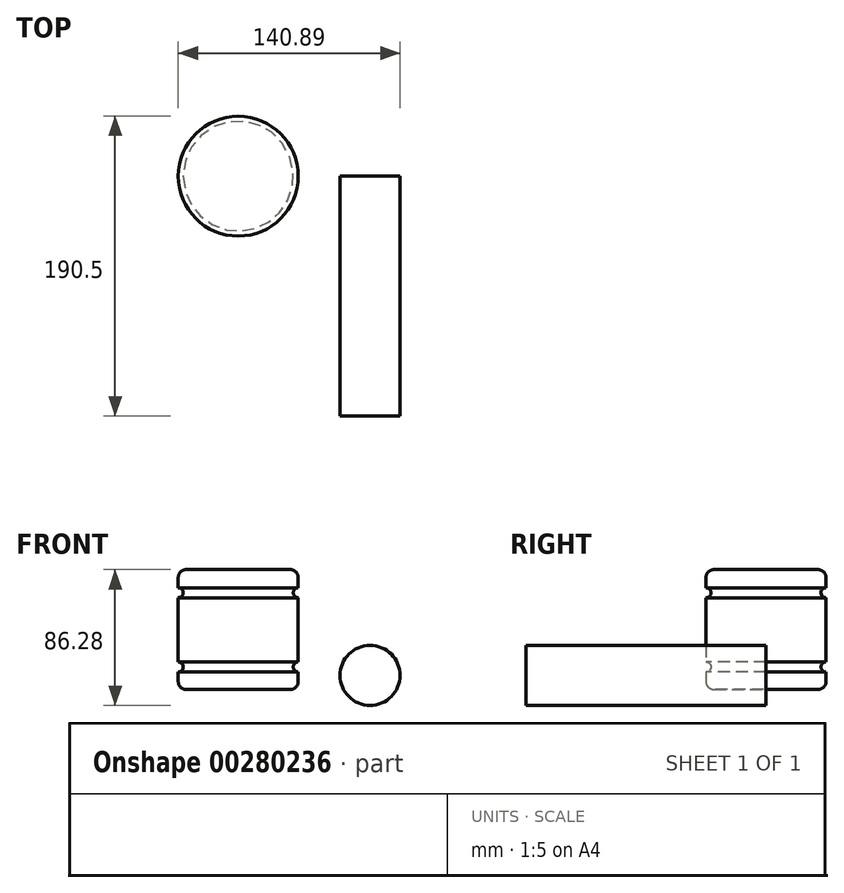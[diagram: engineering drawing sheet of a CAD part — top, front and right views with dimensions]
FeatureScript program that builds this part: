
annotation { "Feature Type Name" : "Feature", "Feature Type Description" : "" }
export const myFeature = defineFeature(function(context is Context, id is Id, definition is map)
    precondition{}
    {
        {
            var Q0;
            Q0=qCreatedBy(makeId("Front.planeOp"),FACE);
            var sketch = newSketch(context, id + "F0", { "sketchPlane" : qUnion([Q0])});
            skLineSegment(sketch, "E0.bottom", {"start": v(0, 0) * mm, "end": v(-38.1, 0) * mm});
            skLineSegment(sketch, "E0.top", {"start": v(0, 76.2) * mm, "end": v(-38.1, 76.2) * mm});
            skLineSegment(sketch, "E0.left", {"start": v(0, 0) * mm, "end": v(0, 76.2) * mm});
            skLineSegment(sketch, "E0.right", {"start": v(-38.1, 0) * mm, "end": v(-38.1, 76.2) * mm});
            skCircle(sketch, "E1", {"center": v(0, 61.49) * mm, "radius": 3.18 * mm});
            skCircle(sketch, "E2", {"center": v(0, 14.32) * mm, "radius": 3.18 * mm});
            skSolve(sketch);
        }
        {
            var Q0;
            {var subQ5=sQuery(id+"F0.wireOp",EDGE,"E0.bottom");Q0=makeQuery(id+"F0.imprint","IMPRINT",FACE,{"disambiguationData":[TD([[makeQuery(id+"F0.imprint","IMPRINT",EDGE,{"derivedFrom":subQ5}),-1.0]])]});}
            var Q1;
            Q1=sQuery(id+"F0.wireOp",EDGE,"E0.right");
            revolve(context, id + "F1", {"entities" : qUnion([Q0]), "axis" : qUnion([Q1]), "revolveType" : RevolveType.FULL});
        }
        {
            var Q0;
            Q0=makeQuery(id+"F1.opRevolve","SWEPT_EDGE",EDGE,{"disambiguationData":[OSD([sQuery(id+"F0.wireOp",EDGE,"E0.top"),sQuery(id+"F0.wireOp",EDGE,"E0.left")])]});
            var Q1;
            Q1=makeQuery(id+"F1.opRevolve","SWEPT_EDGE",EDGE,{"disambiguationData":[OSD([sQuery(id+"F0.wireOp",EDGE,"E0.bottom"),sQuery(id+"F0.wireOp",EDGE,"E0.left")])]});
            fillet(context, id + "F2", {"entities" : qUnion([Q0, Q1]), "radius" : 5.08 * mm, "tangentPropagation" : true, "allowEdgeOverflow" : false});
        }
        {
            var Q0;
            Q0=qCreatedBy(makeId("Front.planeOp"),FACE);
            var sketch = newSketch(context, id + "F3", { "sketchPlane" : qUnion([Q0])});
            skCircle(sketch, "E3", {"center": v(45.64, 8.97) * mm, "radius": 19.05 * mm});
            skSolve(sketch);
        }
        {
            var Q0;
            Q0 = qSketchRegion(id + "F3", true);
            extrude(context, id + "F4", {"entities" : qUnion([Q0]), "depth" : 152.4 * mm});
        }
    });
